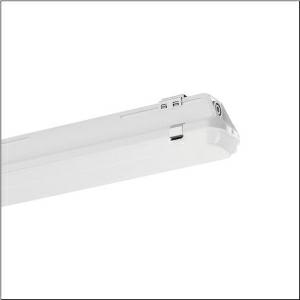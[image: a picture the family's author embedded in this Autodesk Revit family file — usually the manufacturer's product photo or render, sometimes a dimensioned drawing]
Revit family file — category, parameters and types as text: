
# Revit family: monsun_r__12_51fp20ep460h_bb9e
name_source: partatom
category: Lighting Fixtures
units: mm (PartAtom-declared; Revit-internal decimal feet)

## family parameters
Cut with Voids When Loaded = No
Host = Face
Light Source = No
Part Type = Normal
Room Calculation Point = No
Round Connector Dimension = Use Diameter
Shared = No

## types (1)
- --- (1 x LED, 5450 lm, 34.6 W, 4000K)
    Apparent Load = 35 VA
    CIE Flux Codes = 45 75 93 94 100
    Color Rendering = 80
    Color Temperature = 4000K
    Default Elevation = 1800 mm
    Description = Monsun® 12, damp-proof luminaire, chain hanger, primary optical cover: enclosure, of PC, light emission: direct distribution, primary light characteristic: symmetric, installation type: suspended mounting, surface-mounted, horizontal mounting, vertical mounting, LED rated luminous flux: 5.450 lm, light colour: 840, colour temperature: 4000K, control gear: ECG DALI, with terminal, 5-pole, max. 2.5mm², mains connection: 220..240V, AC, 50/60Hz, rated input power: 35W, luminaire housing, of glass-fibre reinforced polyester, uncoated, bright grey, length: 1.590 mm, width: 90 mm, height: 88mm, clip for enclosure, of stainless steel (V2A), ceiling mounting element, of stainless steel (V2A), chain hanger, of stainless steel (V2A), protection rating (complete): IP66, insulation class (complete): insulation class I (protective earthing), certification: CE, ENEC, VDE, protection symbol: D, impact resistance: IK08, permissible ambient temperature for indoor applications: -25..+40°C, standard: EN 50419, EN 60598-2-1, no direct snow, no direct sun, no direct rain, for indoor or canopied outdoor use, corresponds to IFS (International Featured Standards) requirements for safety and quality in the food industry, packaging unit: 1 piece
    Height = 89 mm
    Lamp = 1 x LED
    Lamp Light Flux = 5450 lm
    Lamp Power = 34.6 W
    Lamp count = 1
    Length = 1590 mm
    Luminous efficacy = 158 lm/W
    Manufacturer = Siteco
    ModVariant = No
    Model = 51FP20EP460H
    Mounting Place = Ceiling
    Mounting Type = Pendant
    Number of Poles = 1
    OnlyDefault = Yes
    Power Factor = 1
    Product Name = Monsun® 12
    Product group = damp-proof luminaire | ceiling pendant
    ProductGroupID = 908
    Protection Class = Protection class I
    Protection Degree = IP 66
    RLX_Detail_Level = 1
    RlxData = <blob elided: 92021 chars, md5=b92e4724>
    Socket = socket
    Standby Power = 0 W
    System Light Flux = 5450 lm
    System Power = 35 W
    Type Comments = factory setting: luminous flux: 100 % | dim-lin: 254 | 232 mA
    Type Image = l_1004748.jpg
    URL = http://relux.com
    VarID = @adj_133883
    Voltage = 0 V
    Weight = 0.00 kg
    Width = 90 mm

## geometry (parser evidence)
native form markers: Blend x4, Sweep x14
no freeform markers — native parametric forms only
